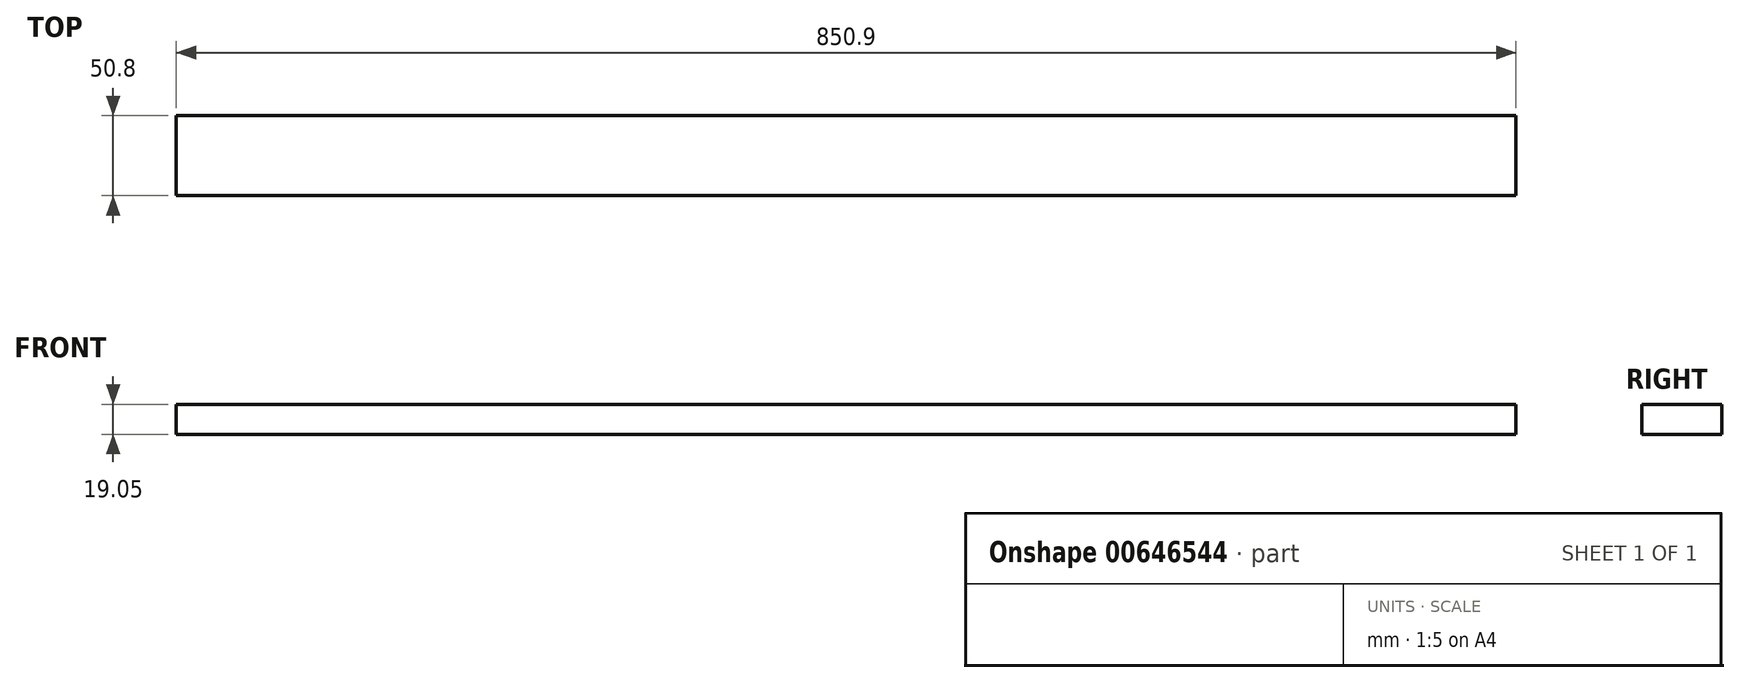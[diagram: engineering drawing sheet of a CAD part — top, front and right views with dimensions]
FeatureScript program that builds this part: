
annotation { "Feature Type Name" : "Feature", "Feature Type Description" : "" }
export const myFeature = defineFeature(function(context is Context, id is Id, definition is map)
    precondition{}
    {
        {
            var Q0;
            Q0=qCreatedBy(makeId("Top.planeOp"),FACE);
            var sketch = newSketch(context, id + "F0", { "sketchPlane" : qUnion([Q0])});
            skLineSegment(sketch, "E0.bottom", {"start": v(-425.45, 25.4) * mm, "end": v(425.45, 25.4) * mm});
            skLineSegment(sketch, "E0.top", {"start": v(-425.45, -25.4) * mm, "end": v(425.45, -25.4) * mm});
            skLineSegment(sketch, "E0.left", {"start": v(-425.45, 25.4) * mm, "end": v(-425.45, -25.4) * mm});
            skLineSegment(sketch, "E0.right", {"start": v(425.45, 25.4) * mm, "end": v(425.45, -25.4) * mm});
            skPoint(sketch, "E0.middle", {"position": v(0, 0) * mm});
            skSolve(sketch);
        }
        {
            var Q0;
            Q0=makeQuery(id+"F0.imprint","IMPRINT",FACE,{"disambiguationData":[TD([[makeQuery(id+"F0.imprint","IMPRINT",EDGE,{"derivedFrom":sQuery(id+"F0.wireOp",EDGE,"E0.bottom")}),-1.0]])]});
            extrude(context, id + "F1", {"entities" : qUnion([Q0]), "depth" : 19.05 * mm, "offsetDistance" : 25.4 * mm});
        }
    });
